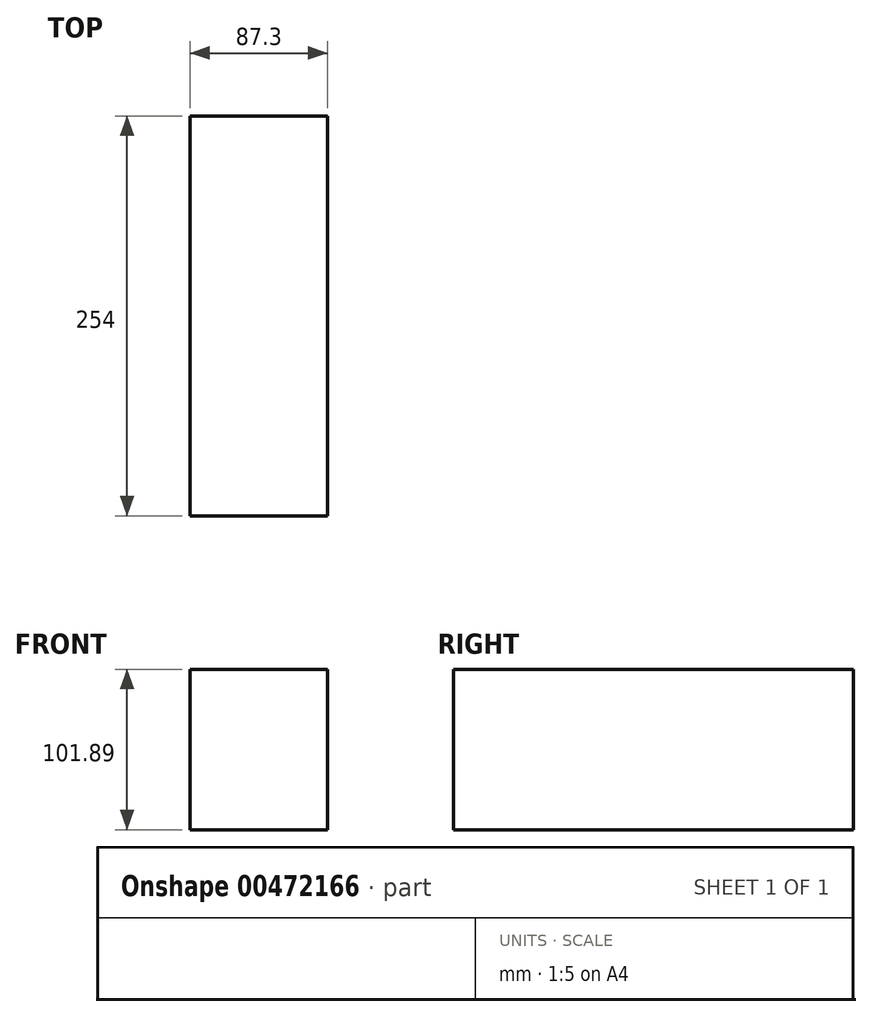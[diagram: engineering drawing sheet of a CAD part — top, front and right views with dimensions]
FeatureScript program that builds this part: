
annotation { "Feature Type Name" : "Feature", "Feature Type Description" : "" }
export const myFeature = defineFeature(function(context is Context, id is Id, definition is map)
    precondition{}
    {
        {
            var Q0;
            Q0=qCreatedBy(makeId("Front.planeOp"),FACE);
            var sketch = newSketch(context, id + "F0", { "sketchPlane" : qUnion([Q0])});
            skLineSegment(sketch, "E0.bottom", {"start": v(-39.02, 64.05) * mm, "end": v(48.28, 64.05) * mm});
            skLineSegment(sketch, "E0.top", {"start": v(-39.02, -37.84) * mm, "end": v(48.28, -37.84) * mm});
            skLineSegment(sketch, "E0.left", {"start": v(-39.02, 64.05) * mm, "end": v(-39.02, -37.84) * mm});
            skLineSegment(sketch, "E0.right", {"start": v(48.28, 64.05) * mm, "end": v(48.28, -37.84) * mm});
            skSolve(sketch);
        }
        {
            var Q0;
            Q0=makeQuery(id+"F0.imprint","IMPRINT",FACE,{"disambiguationData":[TD([[makeQuery(id+"F0.imprint","IMPRINT",EDGE,{"derivedFrom":sQuery(id+"F0.wireOp",EDGE,"E0.bottom")}),-1.0]])]});
            extrude(context, id + "F1", {"entities" : qUnion([Q0]), "depth" : 254 * mm});
        }
    });
